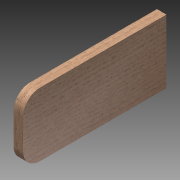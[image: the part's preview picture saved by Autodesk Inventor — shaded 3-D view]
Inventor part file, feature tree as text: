
AUTODESK INVENTOR PART (.ipt)
format: ipt  version: 2013 (Build 170138000, 138)  size: 99,840 bytes
history: native  units: in
note: dims shown in document units (in); Inventor stores cm internally (conversion verified against a paired STEP export)
features: extrude x1, fillet x1, sketch x1
ambient origin geometry x8: Origin, YZ Plane, XZ Plane, XY Plane, X Axis, Y Axis, Z Axis, Center Point
bodies: Solid1 (feature_tree)
feature tree (3):
  extrude  "Extrusion1"  Depth=0.75in
  fillet  "Fillet1"  Radius=11.25in
  sketch  "Sketch1"  dims[d0=5.0in d1=0.75in d2=11.25in d3=0.0in d4=1.3125in]
